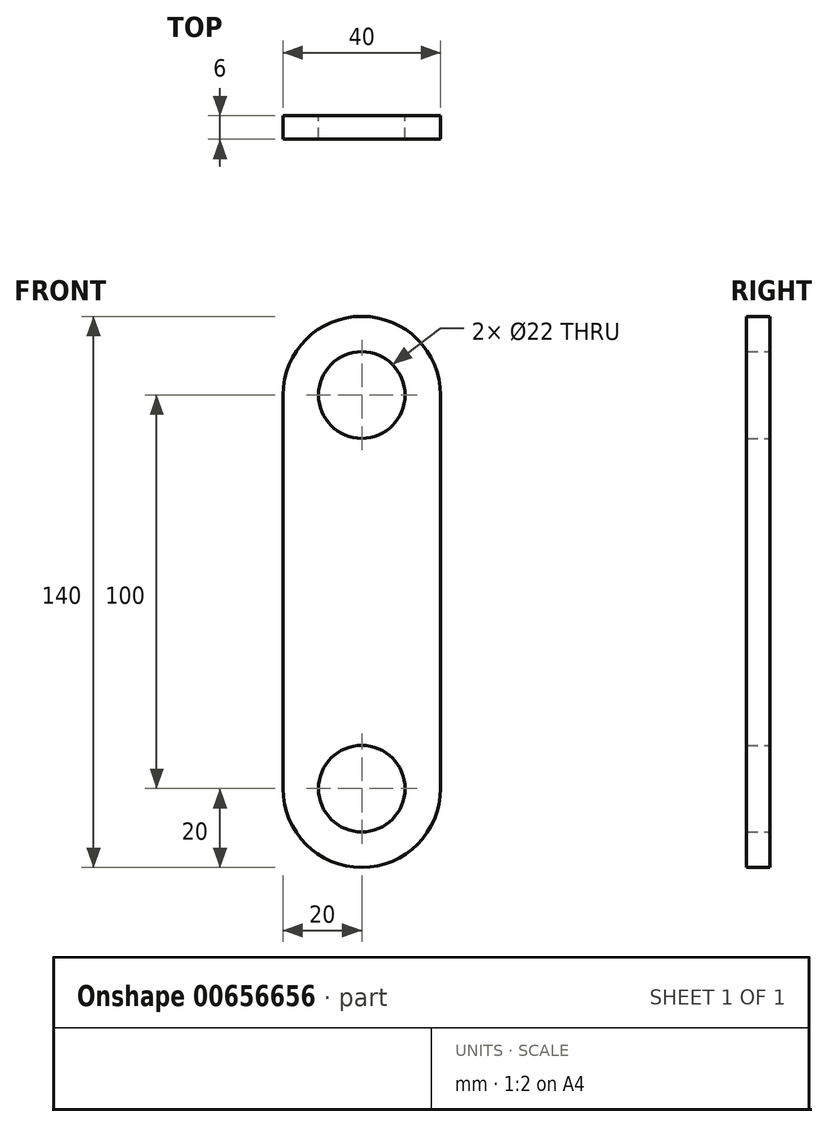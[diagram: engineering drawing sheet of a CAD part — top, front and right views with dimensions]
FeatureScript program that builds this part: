
annotation { "Feature Type Name" : "Feature", "Feature Type Description" : "" }
export const myFeature = defineFeature(function(context is Context, id is Id, definition is map)
    precondition{}
    {
        {
            var Q0;
            Q0=qCreatedBy(makeId("Front.planeOp"),FACE);
            var sketch = newSketch(context, id + "F0", { "sketchPlane" : qUnion([Q0])});
            skCircle(sketch, "E0", {"center": v(0, 0) * mm, "radius": 11 * mm});
            skLineSegment(sketch, "E1", {"start": v(0, 0) * mm, "end": v(0, -100) * mm, "construction": true});
            skCircle(sketch, "E2", {"center": v(0, -100) * mm, "radius": 11 * mm});
            skLineSegment(sketch, "E3.bottom", {"start": v(20, 20) * mm, "end": v(-20, 20) * mm});
            skLineSegment(sketch, "E3.top", {"start": v(20, -120) * mm, "end": v(-20, -120) * mm});
            skLineSegment(sketch, "E3.left", {"start": v(20, 20) * mm, "end": v(20, -120) * mm});
            skLineSegment(sketch, "E3.right", {"start": v(-20, 20) * mm, "end": v(-20, -120) * mm});
            skPoint(sketch, "E3.middle", {"position": v(0, -50) * mm});
            skSolve(sketch);
        }
        {
            var Q0;
            Q0=qSketchRegion(id+"F0",true);
            extrude(context, id + "F1", {"entities" : qUnion([Q0]), "depth" : 6 * mm, "offsetDistance" : 25 * mm});
        }
        {
            var Q0;
            Q0=makeQuery(id+"F1.opExtrude","SWEPT_EDGE",EDGE,{"disambiguationData":[OSD([sQuery(id+"F0.wireOp",EDGE,"E3.bottom"),sQuery(id+"F0.wireOp",EDGE,"E3.left")])]});
            var Q1;
            Q1=makeQuery(id+"F1.opExtrude","SWEPT_EDGE",EDGE,{"disambiguationData":[OSD([sQuery(id+"F0.wireOp",EDGE,"E3.bottom"),sQuery(id+"F0.wireOp",EDGE,"E3.right")])]});
            var Q2;
            Q2=makeQuery(id+"F1.opExtrude","SWEPT_EDGE",EDGE,{"disambiguationData":[OSD([sQuery(id+"F0.wireOp",EDGE,"E3.top"),sQuery(id+"F0.wireOp",EDGE,"E3.right")])]});
            var Q3;
            Q3=makeQuery(id+"F1.opExtrude","SWEPT_EDGE",EDGE,{"disambiguationData":[OSD([sQuery(id+"F0.wireOp",EDGE,"E3.top"),sQuery(id+"F0.wireOp",EDGE,"E3.left")])]});
            fillet(context, id + "F2", {"entities" : qUnion([Q0, Q1, Q2, Q3]), "radius" : 20 * mm, "tangentPropagation" : true, "allowEdgeOverflow" : false});
        }
    });
